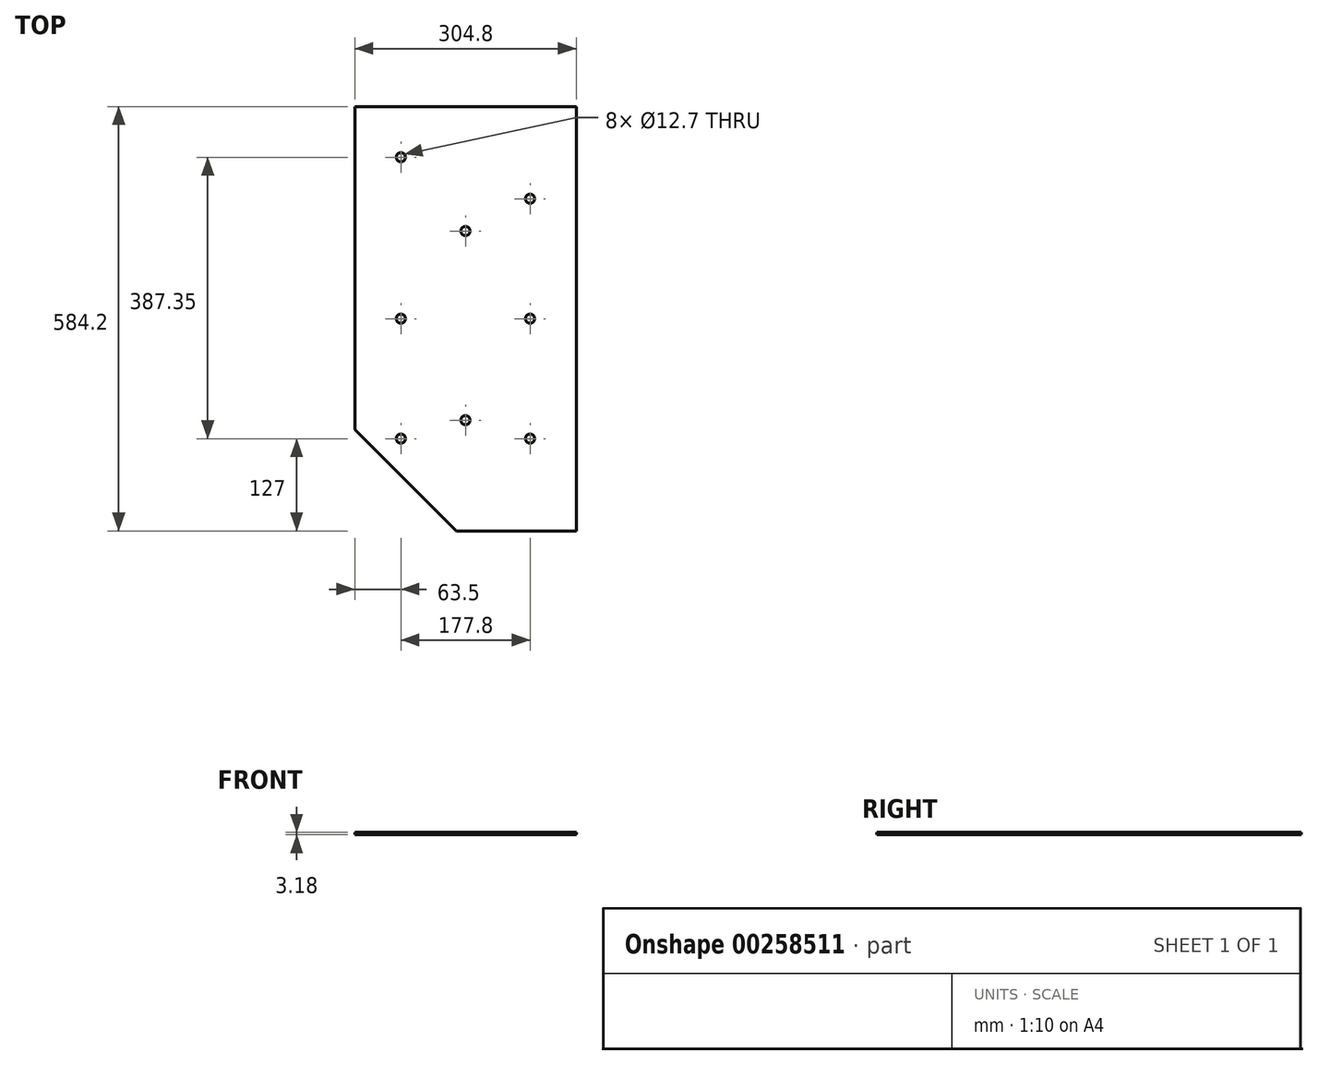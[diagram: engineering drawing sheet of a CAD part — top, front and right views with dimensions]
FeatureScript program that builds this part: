
annotation { "Feature Type Name" : "Feature", "Feature Type Description" : "" }
export const myFeature = defineFeature(function(context is Context, id is Id, definition is map)
    precondition{}
    {
        {
            var Q0;
            Q0=qCreatedBy(makeId("Top.planeOp"),FACE);
            var sketch = newSketch(context, id + "F0", { "sketchPlane" : qUnion([Q0])});
            skLineSegment(sketch, "E0.bottom", {"start": v(152.4, 292.1) * mm, "end": v(-152.4, 292.1) * mm});
            skLineSegment(sketch, "E0.top", {"start": v(12.7, -292.1) * mm, "end": v(-12.7, -292.1) * mm});
            skLineSegment(sketch, "E0.left", {"start": v(152.4, 292.1) * mm, "end": v(152.4, -152.4) * mm});
            skLineSegment(sketch, "E0.right", {"start": v(-152.4, 292.1) * mm, "end": v(-152.4, -152.4) * mm});
            skPoint(sketch, "E0.middle", {"position": v(0, 0) * mm});
            skPoint(sketch, "E1.orphan", {"position": v(152.4, -292.1) * mm});
            skLineSegment(sketch, "E2", {"start": v(-88.9, 292.1) * mm, "end": v(-88.9, 215.9) * mm});
            skLineSegment(sketch, "E3", {"start": v(88.9, 292.1) * mm, "end": v(88.9, 158.75) * mm});
            skLineSegment(sketch, "E4", {"start": v(-95.25, -165.1) * mm, "end": v(-82.55, -165.1) * mm});
            skCircle(sketch, "E5", {"center": v(-88.9, 0) * mm, "radius": 6.35 * mm});
            skCircle(sketch, "E6", {"center": v(88.9, 0) * mm, "radius": 6.35 * mm});
            skCircle(sketch, "E7", {"center": v(-88.9, 222.25) * mm, "radius": 6.35 * mm});
            skCircle(sketch, "E8", {"center": v(88.9, 165.1) * mm, "radius": 6.35 * mm});
            skCircle(sketch, "E9", {"center": v(-88.9, -165.1) * mm, "radius": 6.35 * mm});
            skCircle(sketch, "E10", {"center": v(88.9, -165.1) * mm, "radius": 6.35 * mm});
            skLineSegment(sketch, "E11.trimOffspring", {"start": v(-88.9, 6.35) * mm, "end": v(-88.9, -6.35) * mm});
            skLineSegment(sketch, "E12.trimOffspring", {"start": v(88.9, 6.35) * mm, "end": v(88.9, -6.35) * mm});
            skLineSegment(sketch, "E13.trimOffspring", {"start": v(-88.9, -158.75) * mm, "end": v(-88.9, -215.9) * mm});
            skLineSegment(sketch, "E14.trimOffspring", {"start": v(88.9, -158.75) * mm, "end": v(88.9, -171.45) * mm});
            skLineSegment(sketch, "E15.trimOffspring", {"start": v(82.55, -165.1) * mm, "end": v(95.25, -165.1) * mm});
            skCircle(sketch, "E16", {"center": v(0, 120.65) * mm, "radius": 6.35 * mm});
            skCircle(sketch, "E17", {"center": v(0, -139.7) * mm, "radius": 6.35 * mm});
            skLineSegment(sketch, "E18", {"start": v(12.7, -292.1) * mm, "end": v(152.4, -292.1) * mm});
            skLineSegment(sketch, "E19", {"start": v(152.4, -152.4) * mm, "end": v(152.4, -292.1) * mm});
            skLineSegment(sketch, "E20", {"start": v(-152.4, -152.4) * mm, "end": v(-12.7, -292.1) * mm});
            skPoint(sketch, "E21.trimOffspring.end.orphan", {"position": v(-152.4, -292.1) * mm});
            skPoint(sketch, "E21.trimOffspring.start.orphan", {"position": v(-88.9, -292.1) * mm});
            skSolve(sketch);
        }
        {
            var Q0;
            Q0=qSketchRegion(id+"F0",true);
            extrude(context, id + "F1", {"entities" : qUnion([Q0]), "depth" : 3.17 * mm});
        }
    });
